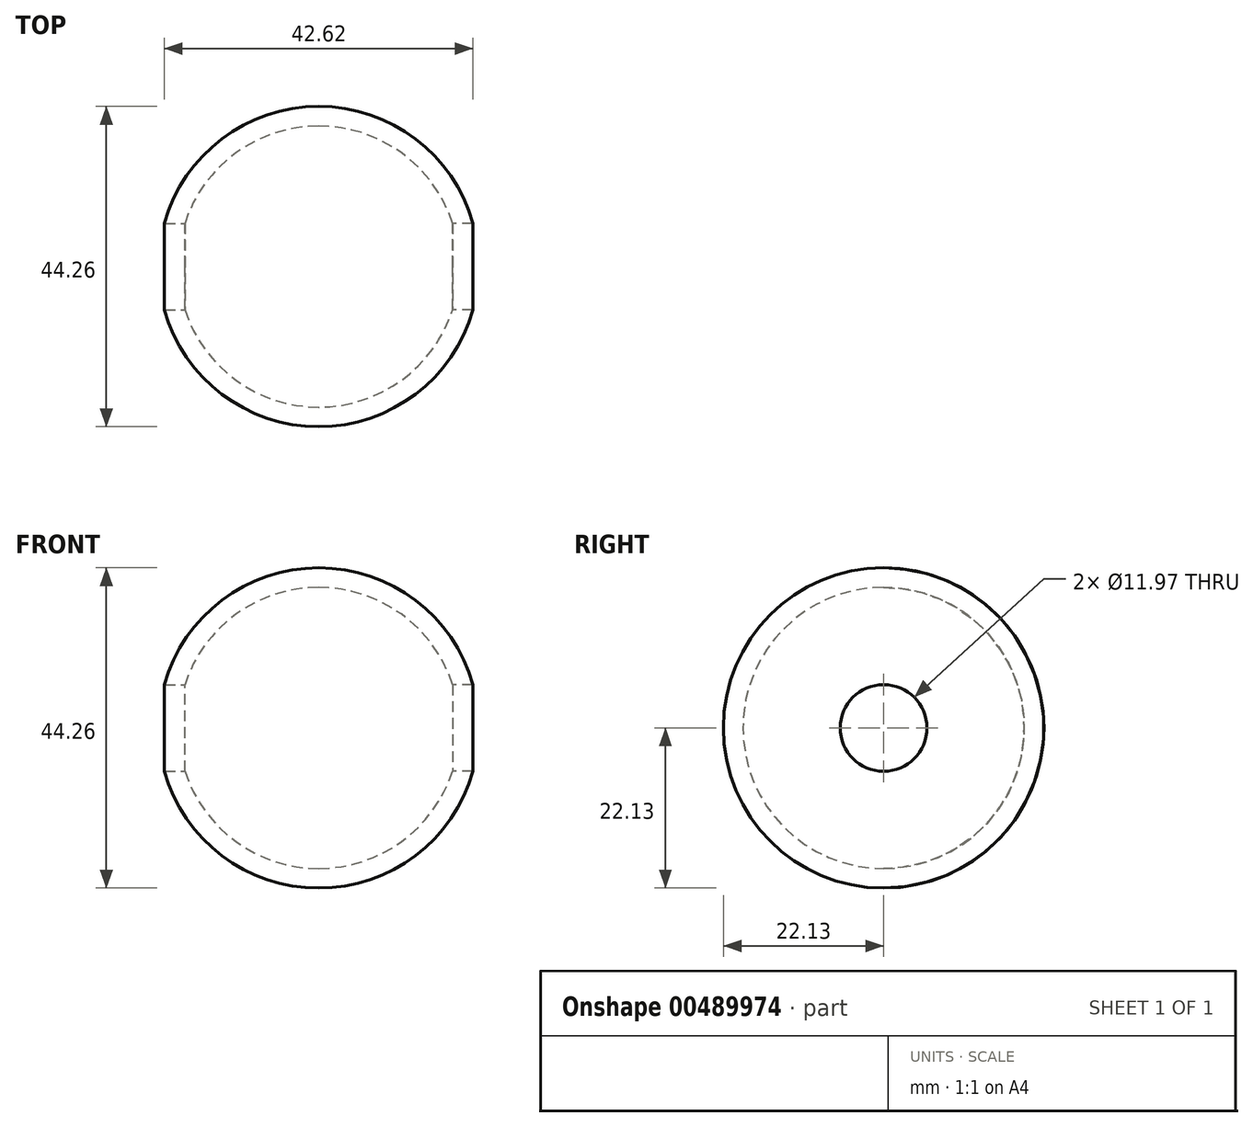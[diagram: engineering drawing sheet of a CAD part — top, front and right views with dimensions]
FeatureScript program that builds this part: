
annotation { "Feature Type Name" : "Feature", "Feature Type Description" : "" }
export const myFeature = defineFeature(function(context is Context, id is Id, definition is map)
    precondition{}
    {
        {
            var Q0;
            Q0=qCreatedBy(makeId("Front.planeOp"),FACE);
            var sketch = newSketch(context, id + "F0", { "sketchPlane" : qUnion([Q0])});
            skLineSegment(sketch, "E0", {"start": v(0, 0) * mm, "end": v(0, 22.13) * mm});
            skArc(sketch, "E1", {"start": v(0, -22.13) * mm, "mid": v(22.13, 0) * mm, "end": v(0, 22.13) * mm});
            skArc(sketch, "E2", {"start": v(0, -19.43) * mm, "mid": v(19.43, 0) * mm, "end": v(0, 19.43) * mm});
            skLineSegment(sketch, "E3", {"start": v(0, 0) * mm, "end": v(0, -22.13) * mm});
            skSolve(sketch);
        }
        {
            var Q0;
            {var subQ0=sQuery(id+"F0.wireOp",EDGE,"E1");Q0=makeQuery(id+"F0.imprint","IMPRINT",FACE,{"disambiguationData":[TD([[makeQuery(id+"F0.imprint","IMPRINT",EDGE,{"derivedFrom":subQ0}),1.0]])]});}
            var Q1;
            Q1=sQuery(id+"F0.wireOp",EDGE,"E0");
            revolve(context, id + "F1", {"entities" : qUnion([Q0]), "axis" : qUnion([Q1]), "revolveType" : RevolveType.FULL});
        }
        {
            var Q0;
            Q0=qCreatedBy(makeId("Right.planeOp"),FACE);
            var sketch = newSketch(context, id + "F2", { "sketchPlane" : qUnion([Q0])});
            skCircle(sketch, "E4", {"center": v(0, 0) * mm, "radius": 5.99 * mm});
            skSolve(sketch);
        }
        {
            var Q0;
            Q0 = qSketchRegion(id + "F2", true);
            extrude(context, id + "F3", {"entities" : qUnion([Q0]), "operationType" : NewBodyOperationType.REMOVE, "oppositeDirection" : true, "depth" : 25.4 * mm});
        }
        {
            var Q0;
            Q0 = qSketchRegion(id + "F2", true);
            extrude(context, id + "F4", {"entities" : qUnion([Q0]), "operationType" : NewBodyOperationType.REMOVE, "oppositeDirection" : true, "depth" : -25.4 * mm});
        }
    });
